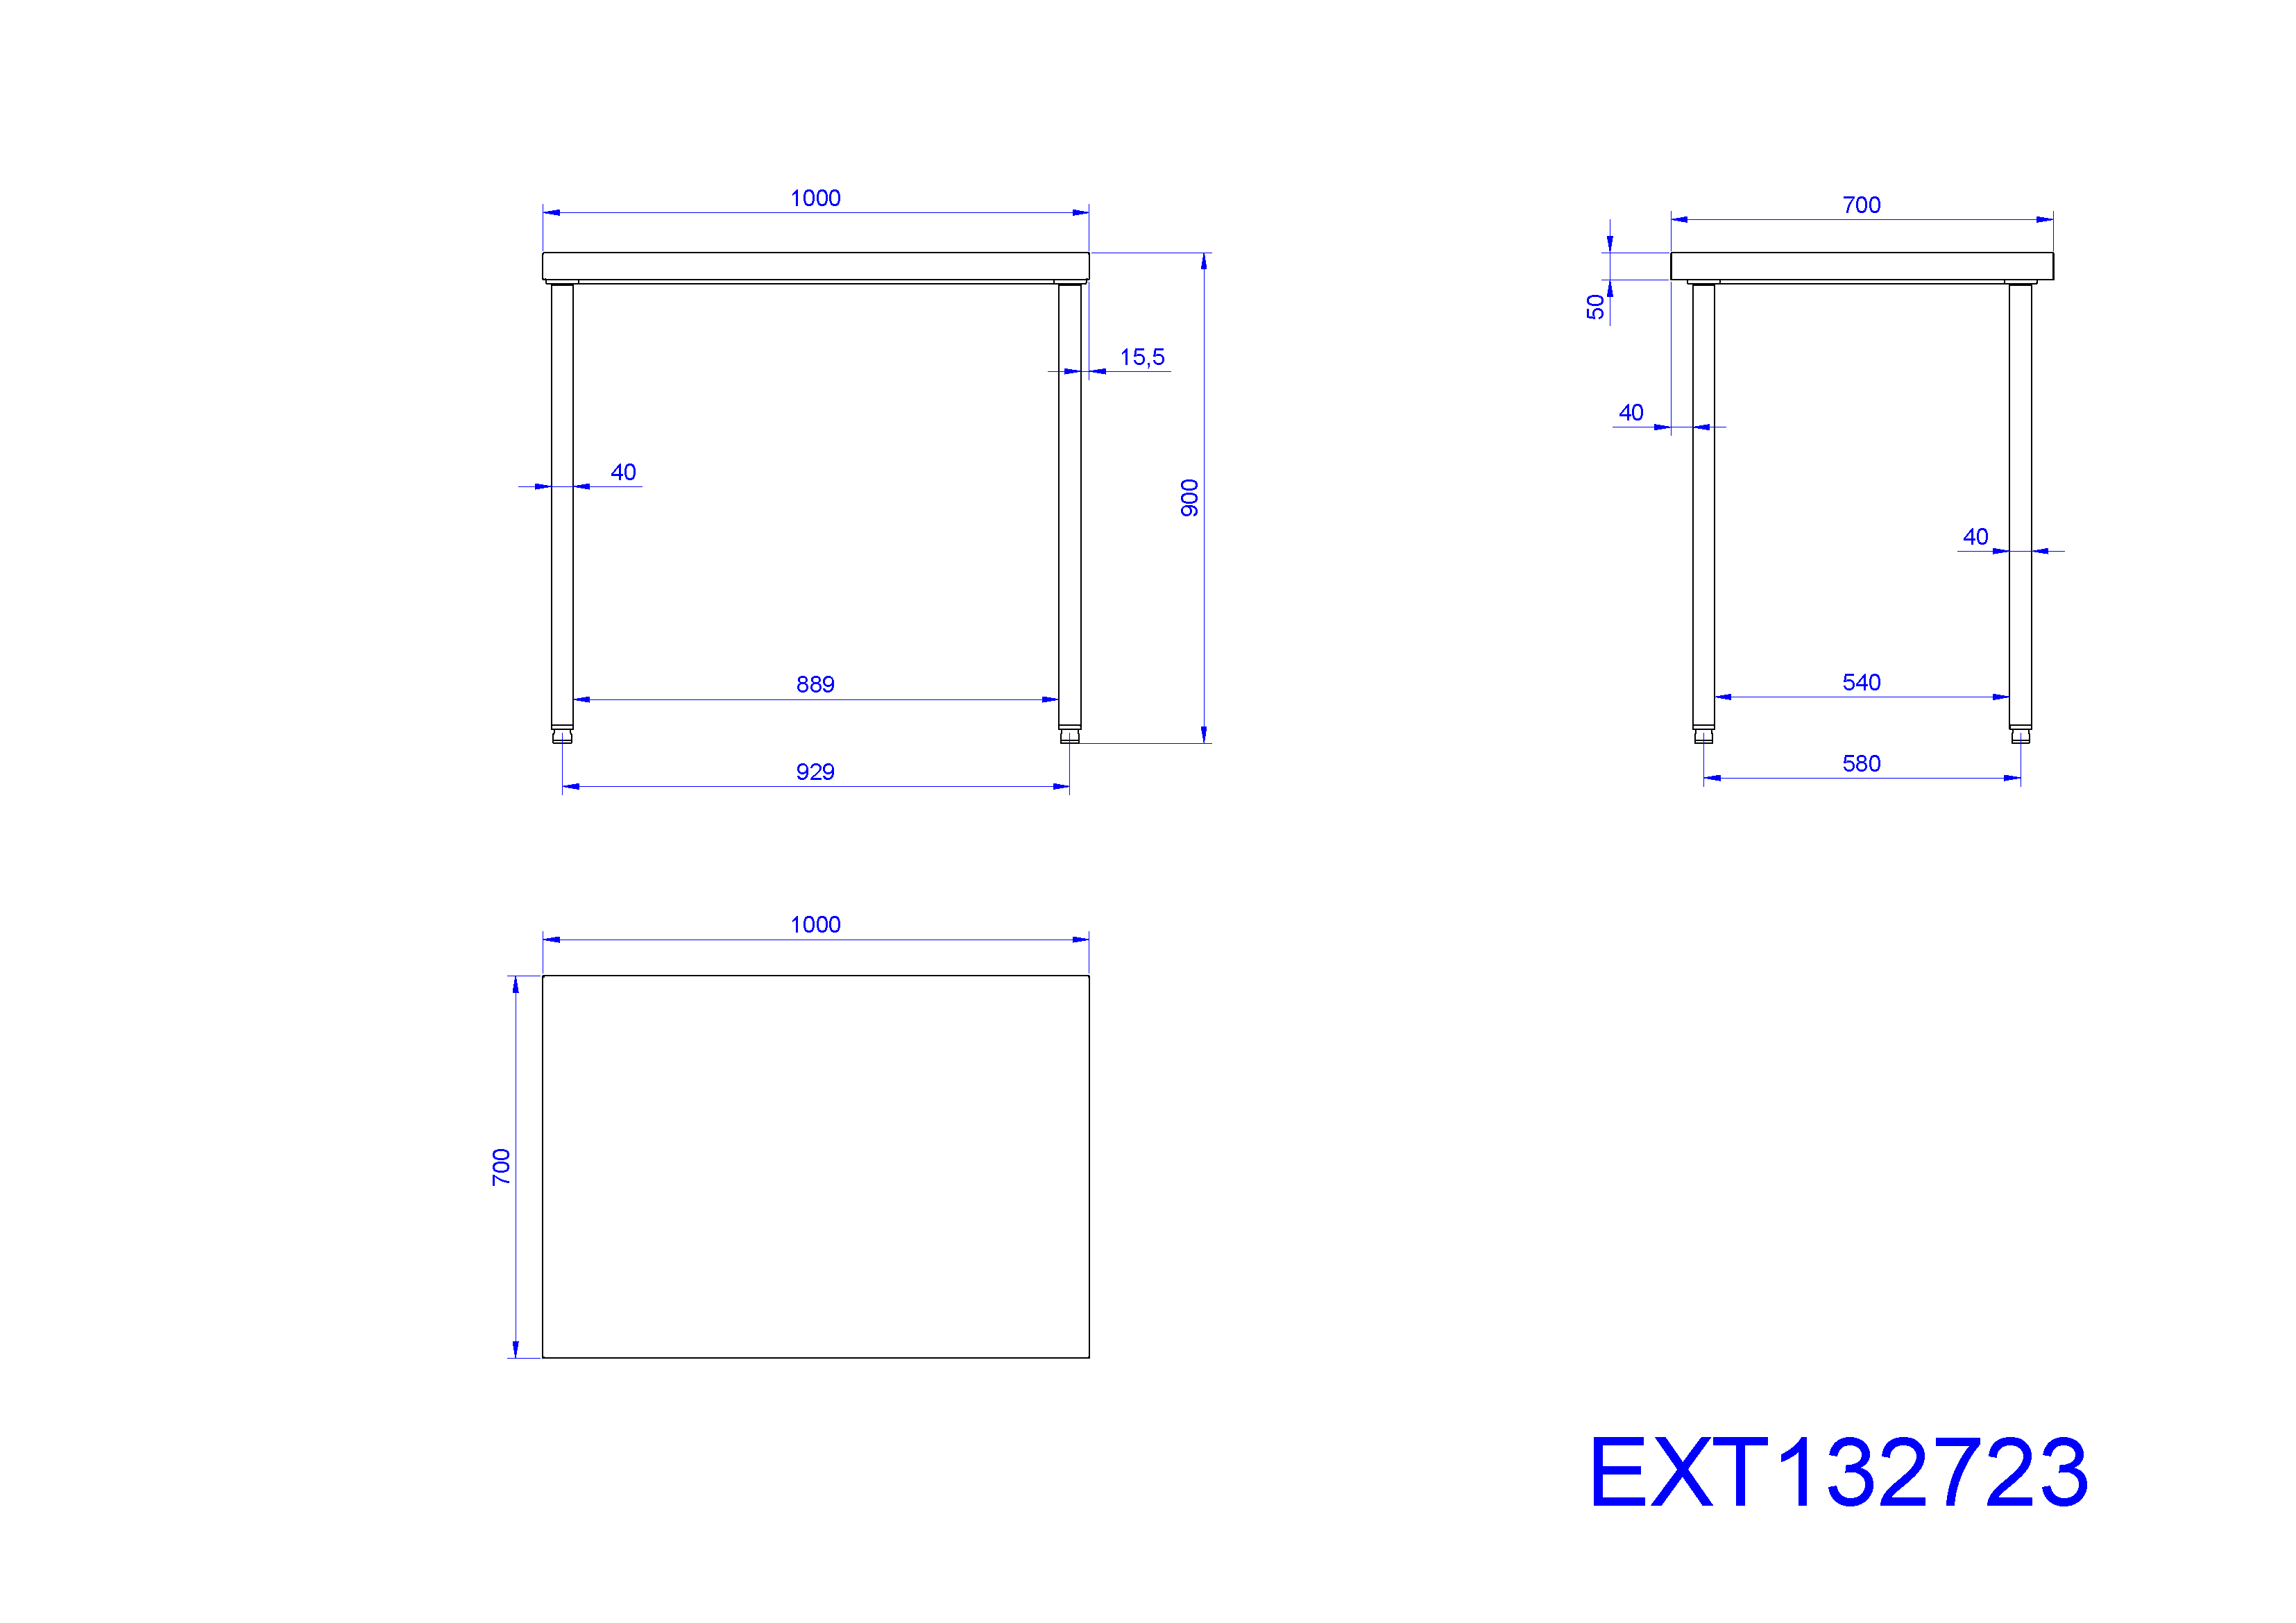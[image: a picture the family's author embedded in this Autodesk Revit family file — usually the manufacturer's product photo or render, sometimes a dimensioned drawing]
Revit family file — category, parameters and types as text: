
# Revit family: QF_ZANUSSI_133050_TG1400EN
name_source: partatom
category: Specialty Equipment
units: mm (PartAtom-declared; Revit-internal decimal feet)

## family parameters
Always vertical = Yes
Cut with Voids When Loaded = No
Part Type = Normal
Room Calculation Point = No
Round Connector Dimension = Use Diameter
Shared = No
Work Plane-Based = No

## types (1)
- Standard
    Accessory = No
    Cold Water Size = 0 mm
    Compressed Air Pressure = 0.0 Pa
    Compressed Air Size = 0 mm
    Compressed Air Volume = 0.0 L/s
    Condensate Return Size = 0 mm
    Cycle = 0 Hz
    Default Elevation = 0 mm  [stored 0 ft]
    Depth Actual = 700 mm  [stored 2.29659 ft]
    Description = WORK TABLE 1400 MM
    Direct Waste Size = 0 mm
    Gas Input Pressure = 0
    Gas KW = 0
    Gas Size = 0 mm
    HP = 0 HP
    Height Actual = 900 mm  [stored 2.95276 ft]
    Hot Water Size = 0 mm
    Item Number = 133050
    Length Actual = 1400 mm  [stored 4.59318 ft]
    Manufacturer = Zanussi
    Model = TG1400EN
    Phase = 0
    Refrigerant Compressor Remote = Yes
    Refrigeration Liquid Line Size = 0 mm  [stored 0 ft]
    Refrigeration Suction Line Size = 0 mm  [stored 0 ft]
    Steam Consumption per Hour = 0
    Steam Supply Maximum Pressure = 0.0 Pa
    Steam Supply Minimum Pressure = 0.0 Pa
    Steam Supply Size = 0 mm
    URL = http://www.zanussiprofessional.com
    URL Manufacturer = http://www.zanussiprofessional.com
    Volts = 0 V
    Watts = 0 W
    Weight = 45.00 kg

note: source unit labels omitted for Gas Input Pressure — the stored unit's dimension contradicts the parameter name (converter mislabeling)

note: [stored X ft] marks values corroborated as IEEE doubles in the binary element streams (Revit-internal decimal feet)

## geometry (parser evidence)
native form markers: Sweep x3
no freeform markers — native parametric forms only
